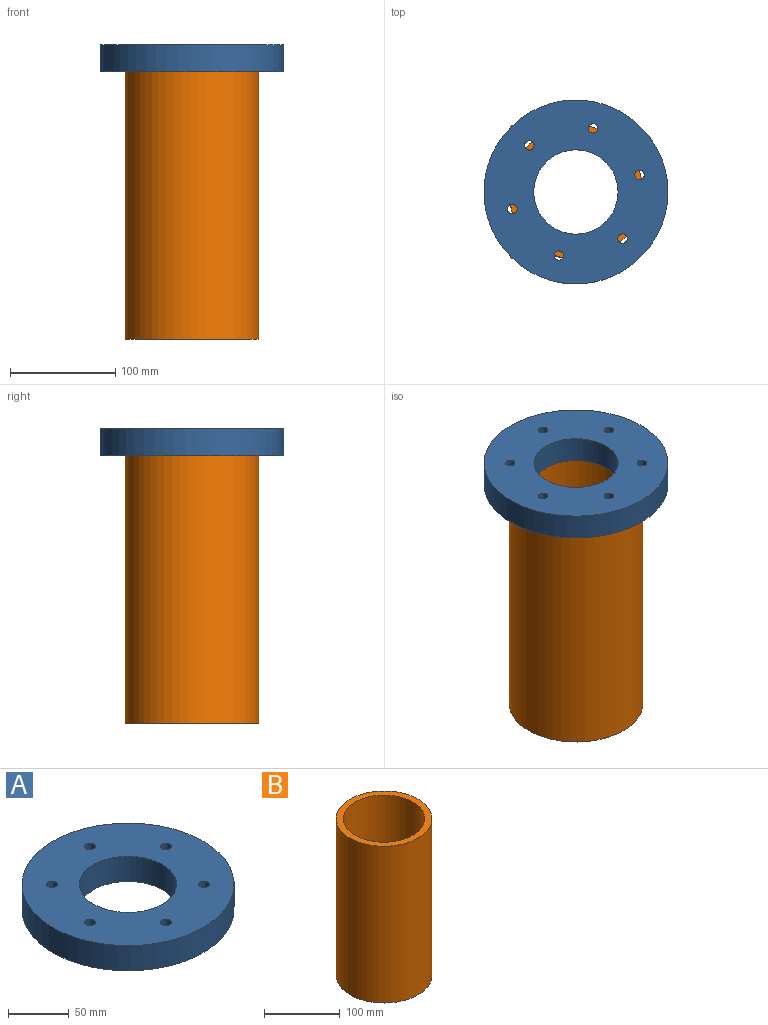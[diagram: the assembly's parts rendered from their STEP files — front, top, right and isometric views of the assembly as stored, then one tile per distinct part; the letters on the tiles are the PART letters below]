
ASSEMBLY  parts=2 mates=1
PART A: 10 faces, bbox 174.6x174.6x25.4 mm
  f0: cylinder r=87.31mm len=174.63mm, axis (0,0,-1), area 13934.5mm2, adj f1,f2
  f1: plane 174.63x174.63mm, normal (0,0,1), area 18541.6mm2, adj f0,f3,f4,f5,f6,f7,f8,f9
  f2: plane 174.63x174.63mm, normal (0,0,-1), area 18541.6mm2, adj f0,f3,f4,f5,f6,f7,f8,f9
  f3: cylinder r=4.5mm len=25.4mm, axis (0,0,1), area 718.2mm2, adj f1,f2
  f4: cylinder r=4.5mm len=25.4mm, axis (0,0,1), area 718.2mm2, adj f1,f2
  f5: cylinder r=4.5mm len=25.4mm, axis (0,0,1), area 718.2mm2, adj f1,f2
  f6: cylinder r=4.5mm len=25.4mm, axis (0,0,1), area 718.2mm2, adj f1,f2
  f7: cylinder r=4.5mm len=25.4mm, axis (0,0,1), area 718.2mm2, adj f1,f2
  f8: cylinder r=4.5mm len=25.4mm, axis (0,0,1), area 718.2mm2, adj f1,f2
  f9: cylinder r=40mm len=80mm, axis (0,0,1), area 6383.7mm2, adj f1,f2
PART B: 4 faces, bbox 127x127x254 mm
  f0: cylinder r=63.5mm len=254mm, axis (0,0,-1), area 101341.5mm2, adj f1,f2
  f1: plane 127x127mm, normal (0,0,1), area 3515.3mm2, adj f0,f3
  f2: plane 127x127mm, normal (0,0,-1), area 3515.3mm2, adj f0,f3
  f3: cylinder r=53.98mm len=254mm, axis (0,0,-1), area 86140.3mm2, adj f1,f2
PLACE A rot(axis=(-0.79,0.55,-0.27),0deg) t=(-478.72,21.12,431.31)mm
PLACE B rot(axis=(-0.79,0.55,-0.27),0deg) t=(-478.72,21.12,304.31)mm
MATE fastened A.f0 <-> B.f0  axis (0,0,-1) through (-478.72,21.12,431.31)mm
